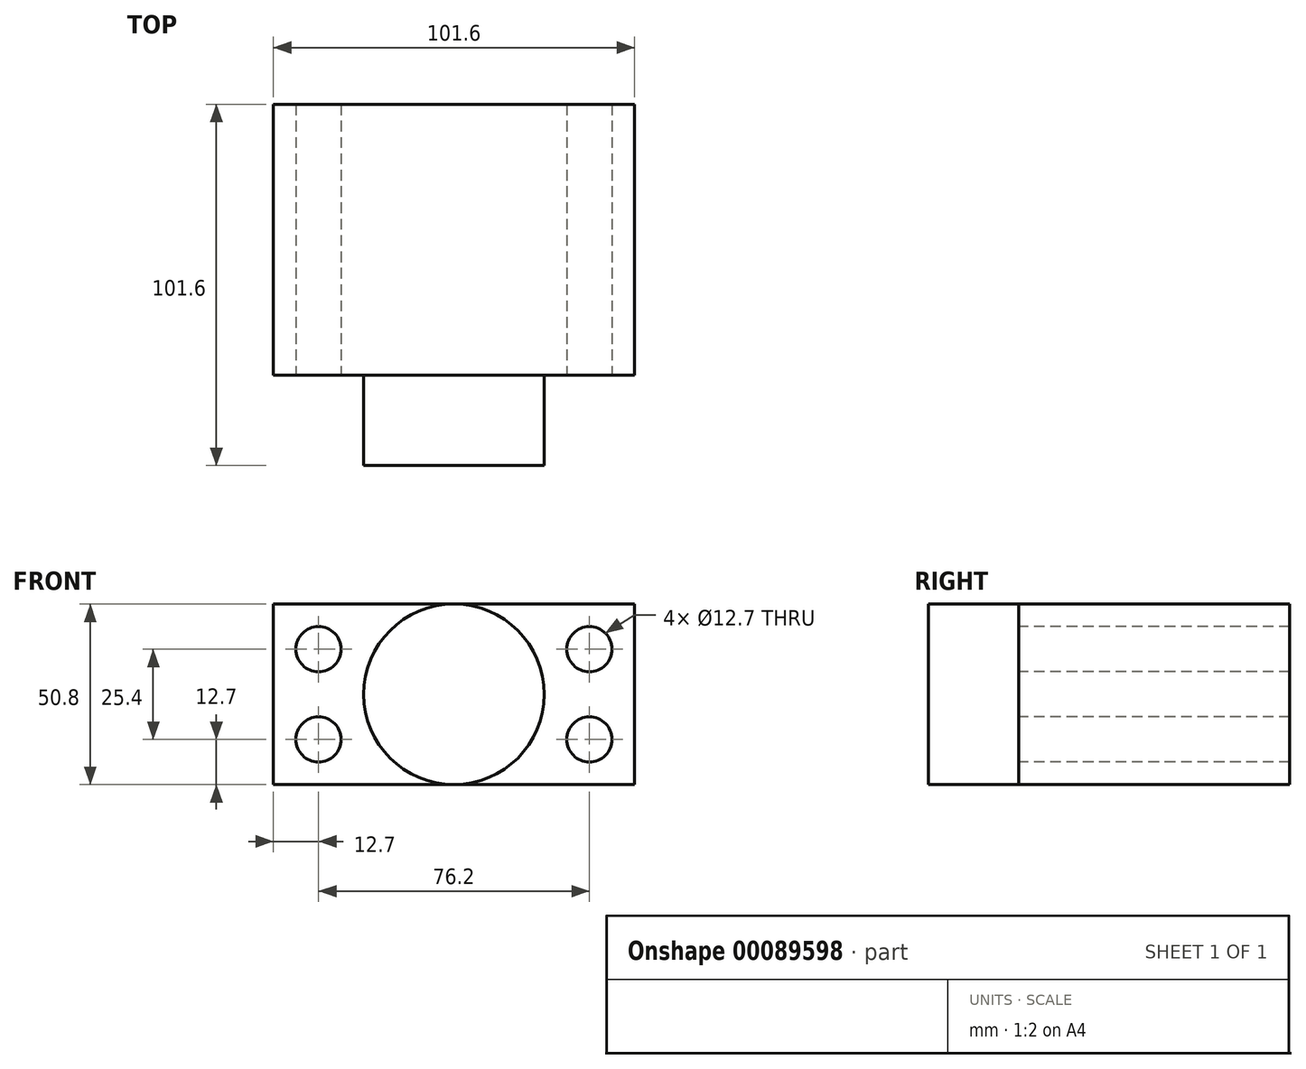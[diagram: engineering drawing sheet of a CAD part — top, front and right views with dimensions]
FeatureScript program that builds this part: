
annotation { "Feature Type Name" : "Feature", "Feature Type Description" : "" }
export const myFeature = defineFeature(function(context is Context, id is Id, definition is map)
    precondition{}
    {
        {
            var Q0;
            Q0=qCreatedBy(makeId("Front.planeOp"),FACE);
            var sketch = newSketch(context, id + "F0", { "sketchPlane" : qUnion([Q0])});
            skLineSegment(sketch, "E0.bottom", {"start": v(-50.8, 25.4) * mm, "end": v(50.8, 25.4) * mm});
            skLineSegment(sketch, "E0.top", {"start": v(-50.8, -25.4) * mm, "end": v(50.8, -25.4) * mm});
            skLineSegment(sketch, "E0.left", {"start": v(-50.8, 25.4) * mm, "end": v(-50.8, -25.4) * mm});
            skLineSegment(sketch, "E0.right", {"start": v(50.8, 25.4) * mm, "end": v(50.8, -25.4) * mm});
            skSolve(sketch);
        }
        {
            var Q0;
            Q0=makeQuery(id+"F0.imprint","IMPRINT",FACE,{"disambiguationData":[TD([[makeQuery(id+"F0.imprint","IMPRINT",EDGE,{"derivedFrom":sQuery(id+"F0.wireOp",EDGE,"E0.bottom")}),-1.0]])]});
            extrude(context, id + "F1", {"entities" : qUnion([Q0]), "depth" : 76.2 * mm});
        }
        {
            var Q0;
            Q0=makeQuery(id+"F1.opExtrude","CAP_FACE",FACE,{"disambiguationData":[OSD([sQuery(id+"F0.wireOp",EDGE,"E0.bottom"),sQuery(id+"F0.wireOp",EDGE,"E0.top"),sQuery(id+"F0.wireOp",EDGE,"E0.left"),sQuery(id+"F0.wireOp",EDGE,"E0.right")])],"isStart":false});
            var sketch = newSketch(context, id + "F2", { "sketchPlane" : qUnion([Q0])});
            skCircle(sketch, "E1", {"center": v(-38.1, 12.7) * mm, "radius": 6.35 * mm});
            skCircle(sketch, "E2", {"center": v(-38.1, -12.7) * mm, "radius": 6.35 * mm});
            skCircle(sketch, "E3.MirrorC", {"center": v(38.1, -12.7) * mm, "radius": 6.35 * mm});
            skCircle(sketch, "E4.MirrorC", {"center": v(38.1, 12.7) * mm, "radius": 6.35 * mm});
            skSolve(sketch);
        }
        {
            var Q0;
            Q0 = qSketchRegion(id + "F2", true);
            extrude(context, id + "F3", {"entities" : qUnion([Q0]), "operationType" : NewBodyOperationType.REMOVE, "endBound" : BoundingType.THROUGH_ALL, "oppositeDirection" : true, "depth" : 25.4 * mm});
        }
        {
            var Q0;
            Q0=qCreatedBy(makeId("Top.planeOp"),FACE);
            var sketch = newSketch(context, id + "F4", { "sketchPlane" : qUnion([Q0])});
            skLineSegment(sketch, "E5.bottom", {"start": v(-25.4, -76.2) * mm, "end": v(0, -76.2) * mm});
            skLineSegment(sketch, "E5.top", {"start": v(-25.4, -101.6) * mm, "end": v(0, -101.6) * mm});
            skLineSegment(sketch, "E5.left", {"start": v(-25.4, -76.2) * mm, "end": v(-25.4, -101.6) * mm});
            skLineSegment(sketch, "E5.right", {"start": v(0, -76.2) * mm, "end": v(0, -101.6) * mm});
            skLineSegment(sketch, "E6", {"start": v(0, 0) * mm, "end": v(0, -108.5) * mm});
            skLineSegment(sketch, "E7", {"start": v(0, -108.5) * mm, "end": v(0, -32.46) * mm, "construction": true});
            skLineSegment(sketch, "E8", {"start": v(0, -32.46) * mm, "end": v(0, -99.48) * mm, "construction": true});
            skSolve(sketch);
        }
        {
            var Q0;
            {var subQ0=sQuery(id+"F4.wireOp",EDGE,"E5.bottom");Q0=makeQuery(id+"F4.imprint","IMPRINT",FACE,{"disambiguationData":[TD([[makeQuery(id+"F4.imprint","IMPRINT",EDGE,{"derivedFrom":subQ0}),-1.0]])]});}
            var Q1;
            Q1=sQuery(id+"F4.wireOp",EDGE,"E6");
            revolve(context, id + "F5", {"operationType" : NewBodyOperationType.ADD, "entities" : qUnion([Q0]), "axis" : qUnion([Q1]), "revolveType" : RevolveType.FULL});
        }
        {
            var Q0;
            Q0=qCreatedBy(makeId("Top.planeOp"),FACE);
            var sketch = newSketch(context, id + "F6", { "sketchPlane" : qUnion([Q0])});
            skLineSegment(sketch, "E9.bottom", {"start": v(-25.4, -95.25) * mm, "end": v(-12.7, -95.25) * mm});
            skLineSegment(sketch, "E9.top", {"start": v(-25.4, -82.55) * mm, "end": v(-12.7, -82.55) * mm});
            skLineSegment(sketch, "E9.right", {"start": v(-12.7, -95.25) * mm, "end": v(-12.7, -82.55) * mm});
            skLineSegment(sketch, "E10", {"start": v(-25.4, -95.25) * mm, "end": v(-25.4, -82.55) * mm});
            skLineSegment(sketch, "E11", {"start": v(0, -101.96) * mm, "end": v(0, -61.56) * mm, "construction": true});
            skSolve(sketch);
        }
    });
